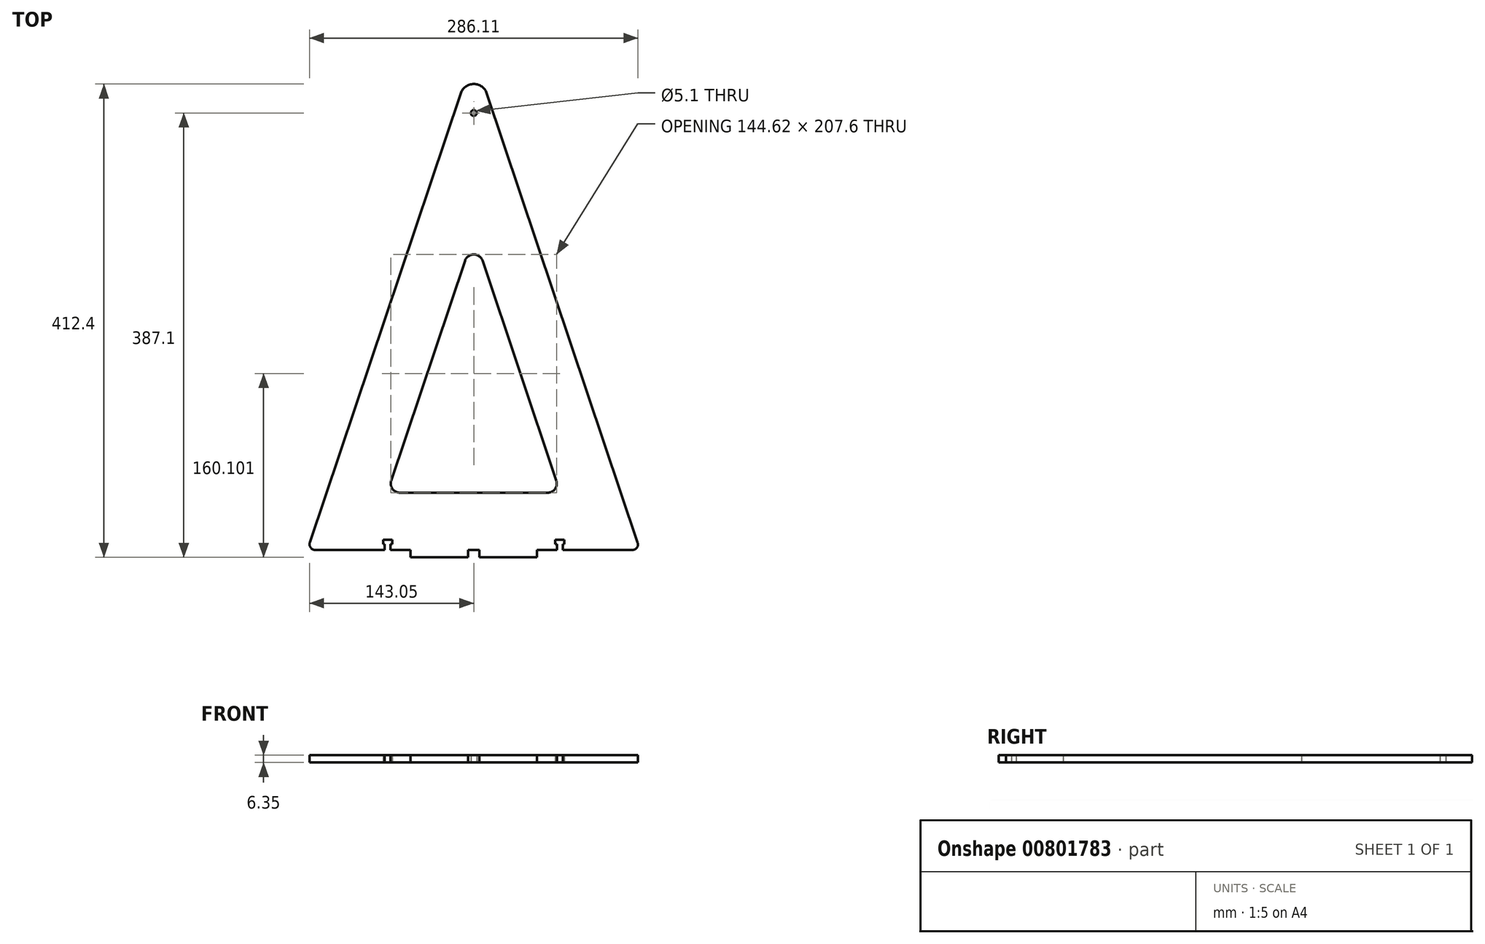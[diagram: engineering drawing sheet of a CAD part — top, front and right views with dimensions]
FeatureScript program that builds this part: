
annotation { "Feature Type Name" : "Feature", "Feature Type Description" : "" }
export const myFeature = defineFeature(function(context is Context, id is Id, definition is map)
    precondition{}
    {
        {
            var Q0;
            Q0=qCreatedBy(makeId("Top.planeOp"),FACE);
            var sketch = newSketch(context, id + "F0", { "sketchPlane" : qUnion([Q0])});
            skLineSegment(sketch, "E0", {"start": v(-142.79, 6.6) * mm, "end": v(-11.38, 397.92) * mm});
            skLineSegment(sketch, "E1", {"start": v(-138.05, 0) * mm, "end": v(-55, 0) * mm});
            skLineSegment(sketch, "E2", {"start": v(-55, 0) * mm, "end": v(-55, -6.3) * mm});
            skLineSegment(sketch, "E3", {"start": v(-55, -6.3) * mm, "end": v(-5, -6.3) * mm});
            skLineSegment(sketch, "E4", {"start": v(-5, -6.3) * mm, "end": v(-5, 0) * mm});
            skLineSegment(sketch, "E5", {"start": v(-5, 0) * mm, "end": v(0, 0) * mm});
            skLineSegment(sketch, "E6.top", {"start": v(-77.55, 9) * mm, "end": v(-72.45, 9) * mm});
            skLineSegment(sketch, "E6.left", {"start": v(-77.55, 0) * mm, "end": v(-77.55, 9) * mm, "construction": true});
            skLineSegment(sketch, "E6.right", {"start": v(-72.45, 0) * mm, "end": v(-72.45, 9) * mm, "construction": true});
            skLineSegment(sketch, "E7.bottom", {"start": v(-75, 9) * mm, "end": v(-79, 9) * mm});
            skLineSegment(sketch, "E7.top", {"start": v(-75, 5) * mm, "end": v(-79, 5) * mm, "construction": true});
            skLineSegment(sketch, "E7.left", {"start": v(-75, 5) * mm, "end": v(-75, 9) * mm, "construction": true});
            skLineSegment(sketch, "E7.right", {"start": v(-79, 5) * mm, "end": v(-79, 9) * mm});
            skLineSegment(sketch, "E8.MirrorCS", {"start": v(-71, 5) * mm, "end": v(-71, 9) * mm});
            skLineSegment(sketch, "E9.MirrorCS", {"start": v(-75, 5) * mm, "end": v(-71, 5) * mm, "construction": true});
            skLineSegment(sketch, "E10.MirrorCS", {"start": v(-75, 9) * mm, "end": v(-71, 9) * mm});
            skLineSegment(sketch, "E11.MirrorCS", {"start": v(142.8, 6.53) * mm, "end": v(11.38, 397.92) * mm});
            skLineSegment(sketch, "E12.MirrorCS", {"start": v(75, 5) * mm, "end": v(75, 9) * mm, "construction": true});
            skLineSegment(sketch, "E13.MirrorCS", {"start": v(77.55, 9) * mm, "end": v(72.45, 9) * mm});
            skLineSegment(sketch, "E14.MirrorCS", {"start": v(79, 5) * mm, "end": v(79, 9) * mm});
            skLineSegment(sketch, "E15.MirrorCS", {"start": v(75, 5) * mm, "end": v(79, 5) * mm, "construction": true});
            skLineSegment(sketch, "E16.MirrorCS", {"start": v(75, 9) * mm, "end": v(79, 9) * mm});
            skLineSegment(sketch, "E17.MirrorCS", {"start": v(71, 5) * mm, "end": v(71, 9) * mm});
            skLineSegment(sketch, "E18.MirrorCS", {"start": v(75, 5) * mm, "end": v(71, 5) * mm, "construction": true});
            skLineSegment(sketch, "E19.MirrorCS", {"start": v(75, 9) * mm, "end": v(71, 9) * mm});
            skLineSegment(sketch, "E20.MirrorCS", {"start": v(5, 0) * mm, "end": v(0, 0) * mm});
            skLineSegment(sketch, "E21.MirrorCS", {"start": v(72.45, 0) * mm, "end": v(72.45, 9) * mm, "construction": true});
            skLineSegment(sketch, "E22.MirrorCS", {"start": v(77.55, 0) * mm, "end": v(77.55, 9) * mm, "construction": true});
            skLineSegment(sketch, "E23.MirrorCS", {"start": v(5, -6.3) * mm, "end": v(5, 0) * mm});
            skLineSegment(sketch, "E24.MirrorCS", {"start": v(55, 0) * mm, "end": v(55, -6.3) * mm});
            skLineSegment(sketch, "E25.MirrorCS", {"start": v(138.1, 0) * mm, "end": v(55, 0) * mm});
            skLineSegment(sketch, "E26.MirrorCS", {"start": v(55, -6.3) * mm, "end": v(5, -6.3) * mm});
            skCircle(sketch, "E27", {"center": v(0, 137) * mm, "radius": 2.55 * mm});
            skLineSegment(sketch, "E28", {"start": v(0, 50) * mm, "end": v(-64.34, 50) * mm});
            skLineSegment(sketch, "E29", {"start": v(-71.92, 60.55) * mm, "end": v(-7.58, 252.15) * mm});
            skLineSegment(sketch, "E30.MirrorCS", {"start": v(71.92, 60.55) * mm, "end": v(7.58, 252.15) * mm});
            skLineSegment(sketch, "E31.MirrorCS", {"start": v(0, 50) * mm, "end": v(64.34, 50) * mm});
            skCircle(sketch, "E32", {"center": v(0, 380.8) * mm, "radius": 2.55 * mm});
            skPoint(sketch, "E33.visualSharp", {"position": v(0, 431.8) * mm});
            skArc(sketch, "E33.filletArc", {"start": v(11.38, 397.92) * mm, "mid": v(0, 406.1) * mm, "end": v(-11.38, 397.92) * mm});
            skPoint(sketch, "E34.visualSharp", {"position": v(-75.47, 50) * mm});
            skArc(sketch, "E34.filletArc", {"start": v(-71.92, 60.55) * mm, "mid": v(-70.84, 53.33) * mm, "end": v(-64.34, 50) * mm});
            skPoint(sketch, "E35.visualSharp", {"position": v(75.47, 50) * mm});
            skArc(sketch, "E35.filletArc", {"start": v(64.34, 50) * mm, "mid": v(70.84, 53.33) * mm, "end": v(71.92, 60.55) * mm});
            skPoint(sketch, "E36.visualSharp", {"position": v(0, 274.73) * mm});
            skArc(sketch, "E36.filletArc", {"start": v(7.58, 252.15) * mm, "mid": v(0, 257.6) * mm, "end": v(-7.58, 252.15) * mm});
            skPoint(sketch, "E37.visualSharp", {"position": v(-145, 0) * mm});
            skPoint(sketch, "E38.visualSharp", {"position": v(145, 0) * mm});
            skArc(sketch, "E38.filletArc", {"start": v(138.1, 0) * mm, "mid": v(142.13, 2.06) * mm, "end": v(142.8, 6.53) * mm});
            skArc(sketch, "E39.filletArc", {"start": v(-142.79, 6.6) * mm, "mid": v(-142.1, 2.08) * mm, "end": v(-138.05, 0) * mm});
            skLineSegment(sketch, "E40", {"start": v(-79, 5) * mm, "end": v(-77.55, 5) * mm});
            skLineSegment(sketch, "E41", {"start": v(-77.55, 5) * mm, "end": v(-77.55, 0) * mm});
            skLineSegment(sketch, "E42", {"start": v(-71, 5) * mm, "end": v(-72.45, 5) * mm});
            skLineSegment(sketch, "E43", {"start": v(-72.45, 5) * mm, "end": v(-72.45, 0) * mm});
            skLineSegment(sketch, "E44", {"start": v(71, 5) * mm, "end": v(72.45, 5) * mm});
            skLineSegment(sketch, "E45", {"start": v(72.45, 5) * mm, "end": v(72.45, 0) * mm});
            skLineSegment(sketch, "E46", {"start": v(79, 5) * mm, "end": v(77.55, 5) * mm});
            skLineSegment(sketch, "E47", {"start": v(77.55, 5) * mm, "end": v(77.55, 0) * mm});
            skSolve(sketch);
        }
        {
            var Q0;
            Q0=makeQuery(id+"F0.imprint","IMPRINT",FACE,{"disambiguationData":[TD([[makeQuery(id+"F0.imprint","IMPRINT",EDGE,{"derivedFrom":sQuery(id+"F0.wireOp",EDGE,"E0")}),-1.0]])]});
            extrude(context, id + "F1", {"entities" : qUnion([Q0]), "depth" : 6.35 * mm, "offsetDistance" : 25 * mm});
        }
    });
